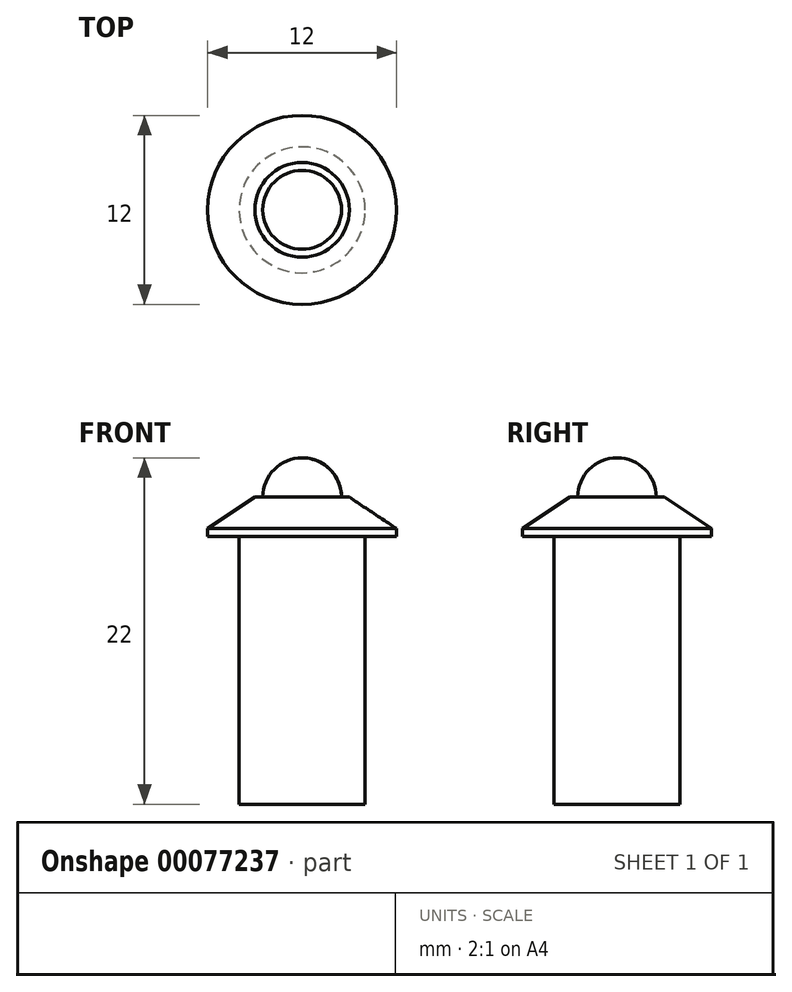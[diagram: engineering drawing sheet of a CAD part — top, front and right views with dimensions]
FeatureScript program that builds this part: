
annotation { "Feature Type Name" : "Feature", "Feature Type Description" : "" }
export const myFeature = defineFeature(function(context is Context, id is Id, definition is map)
    precondition{}
    {
        {
            var Q0;
            Q0=qCreatedBy(makeId("Front.planeOp"),FACE);
            var sketch = newSketch(context, id + "F0", { "sketchPlane" : qUnion([Q0])});
            skLineSegment(sketch, "E0", {"start": v(0, 2.5) * mm, "end": v(0, -17) * mm});
            skLineSegment(sketch, "E1", {"start": v(0, -17) * mm, "end": v(-4, -17) * mm});
            skLineSegment(sketch, "E2", {"start": v(-4, -17) * mm, "end": v(-4, 0) * mm});
            skLineSegment(sketch, "E3", {"start": v(-4, 0) * mm, "end": v(-6, 0) * mm});
            skLineSegment(sketch, "E4", {"start": v(-6, 0) * mm, "end": v(-6, 0.5) * mm});
            skLineSegment(sketch, "E5", {"start": v(-6, 0.5) * mm, "end": v(-3, 2.5) * mm});
            skLineSegment(sketch, "E6", {"start": v(-3, 2.5) * mm, "end": v(0, 2.5) * mm});
            skSolve(sketch);
        }
        {
            var Q0;
            Q0 = qSketchRegion(id + "F0", true);
            var Q1;
            Q1=sQuery(id+"F0.wireOp",EDGE,"E0");
            revolve(context, id + "F1", {"entities" : qUnion([Q0]), "axis" : qUnion([Q1]), "revolveType" : RevolveType.FULL});
        }
        {
            var Q0;
            Q0=qCreatedBy(makeId("Front.planeOp"),FACE);
            var sketch = newSketch(context, id + "F2", { "sketchPlane" : qUnion([Q0])});
            skLineSegment(sketch, "E7", {"start": v(0, 2.5) * mm, "end": v(0, 5) * mm});
            skLineSegment(sketch, "E8", {"start": v(0, 2.5) * mm, "end": v(-2.5, 2.5) * mm});
            skArc(sketch, "E9", {"start": v(-2.5, 2.5) * mm, "mid": v(-1.77, 4.27) * mm, "end": v(0, 5) * mm});
            skSolve(sketch);
        }
        {
            var Q0;
            Q0 = qSketchRegion(id + "F2", true);
            var Q1;
            Q1=sQuery(id+"F2.wireOp",EDGE,"E7");
            revolve(context, id + "F3", {"entities" : qUnion([Q0]), "axis" : qUnion([Q1]), "revolveType" : RevolveType.FULL});
        }
    });
